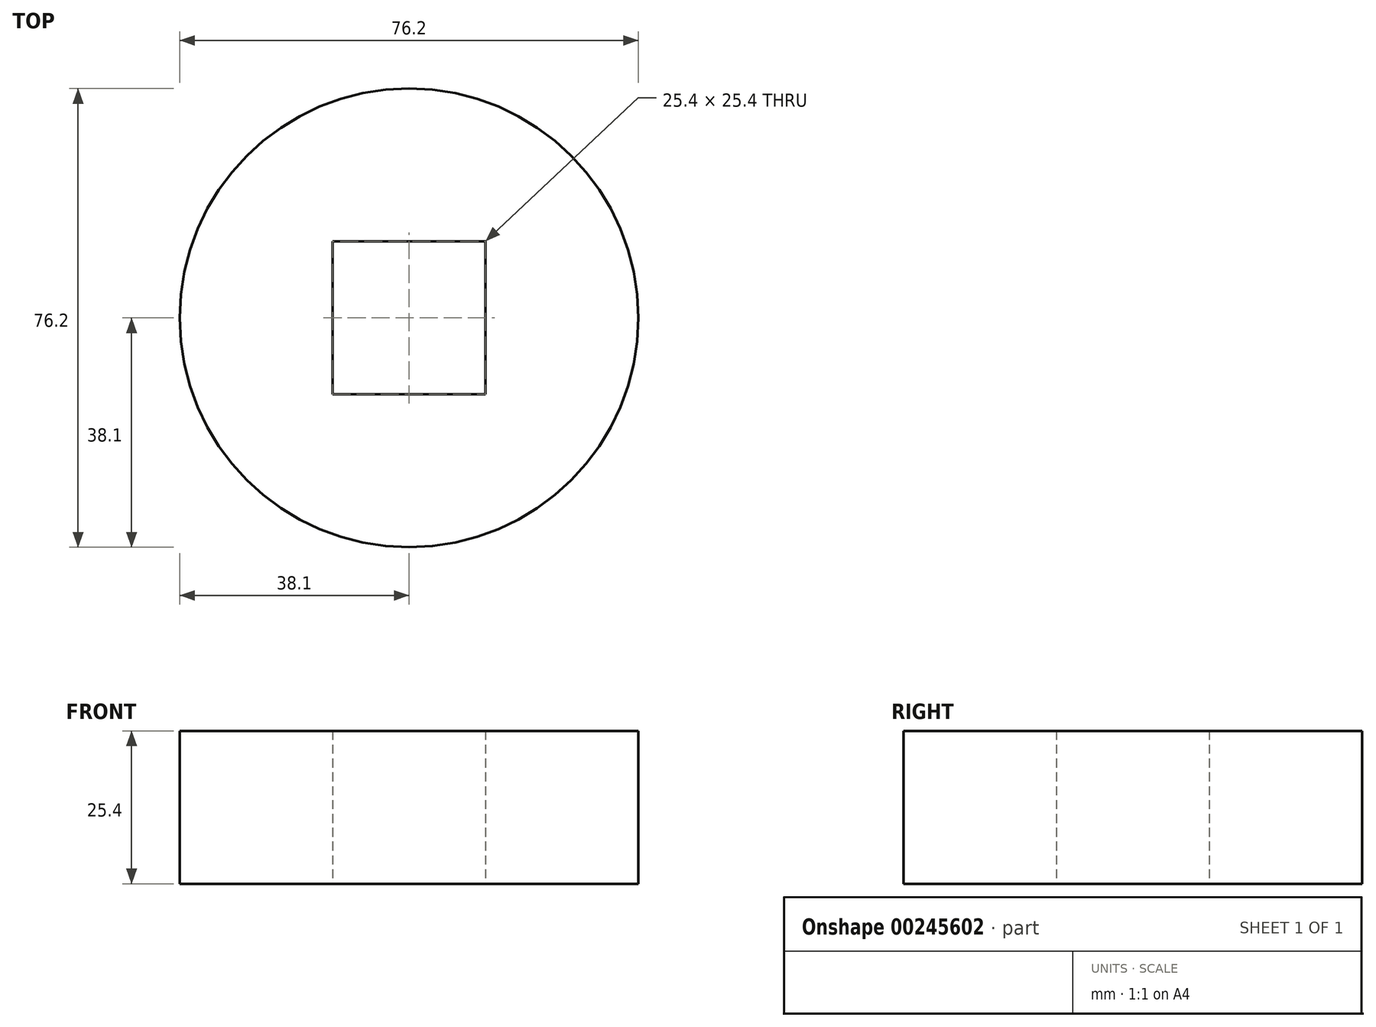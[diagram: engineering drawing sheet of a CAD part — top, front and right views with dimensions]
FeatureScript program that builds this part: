
annotation { "Feature Type Name" : "Feature", "Feature Type Description" : "" }
export const myFeature = defineFeature(function(context is Context, id is Id, definition is map)
    precondition{}
    {
        {
            var Q0;
            Q0=qCreatedBy(makeId("Top.planeOp"),FACE);
            var sketch = newSketch(context, id + "F0", { "sketchPlane" : qUnion([Q0])});
            skCircle(sketch, "E0", {"center": v(0, 0) * mm, "radius": 38.1 * mm});
            skSolve(sketch);
        }
        {
            var Q0;
            Q0 = qSketchRegion(id + "F0", true);
            extrude(context, id + "F1", {"entities" : qUnion([Q0]), "endBound" : BoundingType.SYMMETRIC, "depth" : 25.4 * mm});
        }
        {
            var Q0;
            Q0=qCreatedBy(makeId("Top.planeOp"),FACE);
            var sketch = newSketch(context, id + "F2", { "sketchPlane" : qUnion([Q0])});
            skLineSegment(sketch, "E1.bottom", {"start": v(-12.7, 12.7) * mm, "end": v(12.7, 12.7) * mm});
            skLineSegment(sketch, "E1.top", {"start": v(-12.7, -12.7) * mm, "end": v(12.7, -12.7) * mm});
            skLineSegment(sketch, "E1.left", {"start": v(-12.7, 12.7) * mm, "end": v(-12.7, -12.7) * mm});
            skLineSegment(sketch, "E1.right", {"start": v(12.7, 12.7) * mm, "end": v(12.7, -12.7) * mm});
            skPoint(sketch, "E1.middle", {"position": v(0, 0) * mm});
            skSolve(sketch);
        }
        {
            var Q0;
            Q0 = qSketchRegion(id + "F2", true);
            extrude(context, id + "F3", {"entities" : qUnion([Q0]), "endBound" : BoundingType.SYMMETRIC, "depth" : 50.8 * mm});
        }
        {
            var Q0;
            Q0=makeQuery(id+"F3.opExtrude","SWEPT_BODY",BODY,{"disambiguationData":[OSD([sQuery(id+"F2.wireOp",EDGE,"E1.bottom"),sQuery(id+"F2.wireOp",EDGE,"E1.top"),sQuery(id+"F2.wireOp",EDGE,"E1.left"),sQuery(id+"F2.wireOp",EDGE,"E1.right")])]});
            var Q1;
            Q1=makeQuery(id+"F1.opExtrude","SWEPT_BODY",BODY,{"disambiguationData":[OSD([sQuery(id+"F0.wireOp",EDGE,"E0")])]});
            var Q2;
            Q2=makeQuery(id+"F3.opExtrude","SWEPT_BODY",BODY,{"disambiguationData":[OSD([sQuery(id+"F2.wireOp",EDGE,"E1.bottom"),sQuery(id+"F2.wireOp",EDGE,"E1.top"),sQuery(id+"F2.wireOp",EDGE,"E1.left"),sQuery(id+"F2.wireOp",EDGE,"E1.right")])]});
            booleanBodies(context, id + "F4", {"operationType" : BooleanOperationType.SUBTRACTION, "tools" : qUnion([Q0]), "targets" : qUnion([Q1, Q2]), "keepTools" : true});
        }
    });
